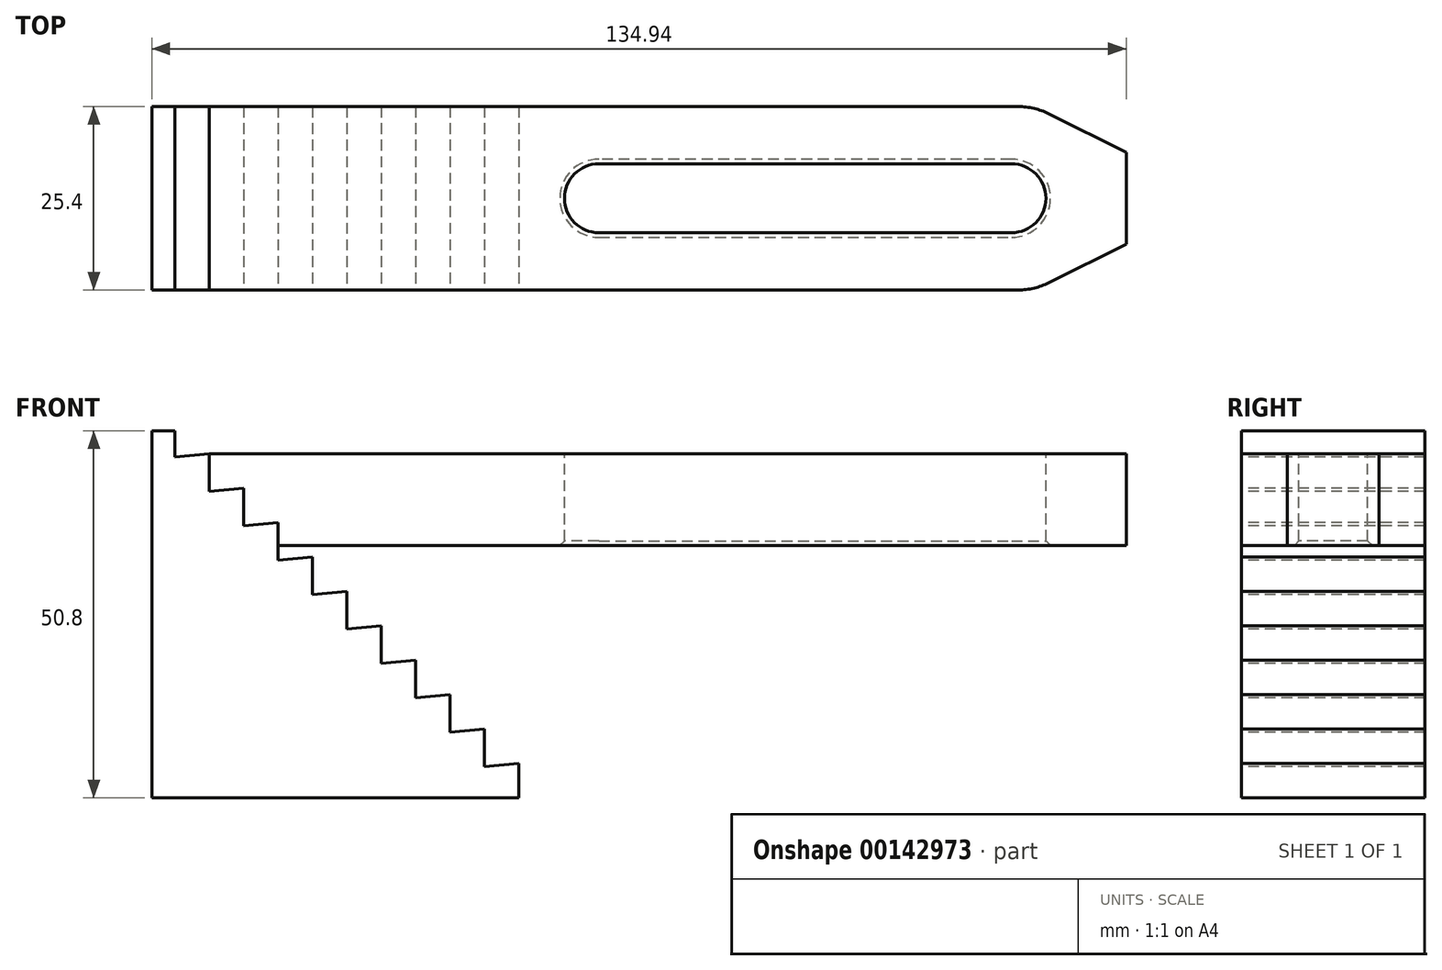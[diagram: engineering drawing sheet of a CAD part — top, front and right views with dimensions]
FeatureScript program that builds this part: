
annotation { "Feature Type Name" : "Feature", "Feature Type Description" : "" }
export const myFeature = defineFeature(function(context is Context, id is Id, definition is map)
    precondition{}
    {
        {
            var Q0;
            Q0=qCreatedBy(makeId("Top.planeOp"),FACE);
            var sketch = newSketch(context, id + "F0", { "sketchPlane" : qUnion([Q0])});
            skLineSegment(sketch, "E0.bottom", {"start": v(0, 0) * mm, "end": v(0, 0) * mm});
            skLineSegment(sketch, "E0.top", {"start": v(0, 0) * mm, "end": v(0, 0) * mm});
            skLineSegment(sketch, "E0.left", {"start": v(0, 0) * mm, "end": v(0, 0) * mm});
            skLineSegment(sketch, "E0.right", {"start": v(0, 0) * mm, "end": v(0, 0) * mm});
            skPoint(sketch, "E0.middle", {"position": v(0, 0) * mm});
            skLineSegment(sketch, "E1.bottom", {"start": v(25.4, 12.7) * mm, "end": v(-25.4, 12.7) * mm});
            skLineSegment(sketch, "E1.top", {"start": v(25.4, -12.7) * mm, "end": v(-25.4, -12.7) * mm});
            skLineSegment(sketch, "E1.left", {"start": v(25.4, 12.7) * mm, "end": v(25.4, -12.7) * mm});
            skLineSegment(sketch, "E1.right", {"start": v(-25.4, 12.7) * mm, "end": v(-25.4, -12.7) * mm});
            skSolve(sketch);
        }
        {
            var Q0;
            Q0 = qSketchRegion(id + "F0", true);
            extrude(context, id + "F1", {"entities" : qUnion([Q0]), "depth" : 50.8 * mm});
        }
        {
            var Q0;
            Q0=makeQuery(id+"F1.opExtrude","SWEPT_FACE",FACE,{"disambiguationData":[OSD([sQuery(id+"F0.wireOp",EDGE,"E1.top")])]});
            var sketch = newSketch(context, id + "F6", { "sketchPlane" : qUnion([Q0])});
            skLineSegment(sketch, "E2", {"start": v(-34.16, 4.76) * mm, "end": v(35.54, 4.76) * mm, "construction": true});
            skLineSegment(sketch, "E3", {"start": v(25.4, 4.76) * mm, "end": v(20.64, 4.35) * mm});
            skLineSegment(sketch, "E4.0.1.0", {"start": v(25.4, 9.53) * mm, "end": v(20.64, 9.1) * mm});
            skLineSegment(sketch, "E4.0.2.0", {"start": v(25.4, 14.29) * mm, "end": v(20.64, 13.87) * mm});
            skLineSegment(sketch, "E4.0.3.0", {"start": v(25.4, 19.05) * mm, "end": v(20.64, 18.63) * mm});
            skLineSegment(sketch, "E4.0.4.0", {"start": v(25.4, 23.81) * mm, "end": v(20.64, 23.4) * mm});
            skLineSegment(sketch, "E4.0.5.0", {"start": v(25.4, 28.58) * mm, "end": v(20.64, 28.16) * mm});
            skLineSegment(sketch, "E4.0.6.0", {"start": v(25.4, 33.34) * mm, "end": v(20.64, 32.92) * mm});
            skLineSegment(sketch, "E4.0.7.0", {"start": v(25.4, 38.1) * mm, "end": v(20.64, 37.68) * mm});
            skLineSegment(sketch, "E4.0.8.0", {"start": v(25.4, 42.86) * mm, "end": v(20.64, 42.45) * mm});
            skLineSegment(sketch, "E4.0.9.0", {"start": v(25.4, 47.63) * mm, "end": v(20.64, 47.2) * mm});
            skLineSegment(sketch, "E4.0.10.0", {"start": v(25.4, 52.39) * mm, "end": v(20.64, 51.97) * mm});
            skLineSegment(sketch, "E4.0.11.0", {"start": v(25.4, 57.15) * mm, "end": v(20.64, 56.73) * mm});
            skLineSegment(sketch, "E4.0.12.0", {"start": v(25.4, 61.91) * mm, "end": v(20.64, 61.5) * mm});
            skLineSegment(sketch, "E4.0.13.0", {"start": v(25.4, 66.68) * mm, "end": v(20.64, 66.26) * mm});
            skLineSegment(sketch, "E4.0.14.0", {"start": v(25.4, 71.44) * mm, "end": v(20.64, 71.02) * mm});
            skLineSegment(sketch, "E4.1.0.0", {"start": v(20.64, 4.76) * mm, "end": v(15.88, 4.35) * mm});
            skLineSegment(sketch, "E4.1.1.0", {"start": v(20.64, 9.53) * mm, "end": v(15.88, 9.1) * mm});
            skLineSegment(sketch, "E4.1.2.0", {"start": v(20.64, 14.29) * mm, "end": v(15.88, 13.87) * mm});
            skLineSegment(sketch, "E4.1.3.0", {"start": v(20.64, 19.05) * mm, "end": v(15.88, 18.63) * mm});
            skLineSegment(sketch, "E4.1.4.0", {"start": v(20.64, 23.81) * mm, "end": v(15.88, 23.4) * mm});
            skLineSegment(sketch, "E4.1.5.0", {"start": v(20.64, 28.58) * mm, "end": v(15.88, 28.16) * mm});
            skLineSegment(sketch, "E4.1.6.0", {"start": v(20.64, 33.34) * mm, "end": v(15.88, 32.92) * mm});
            skLineSegment(sketch, "E4.1.7.0", {"start": v(20.64, 38.1) * mm, "end": v(15.88, 37.68) * mm});
            skLineSegment(sketch, "E4.1.8.0", {"start": v(20.64, 42.86) * mm, "end": v(15.88, 42.45) * mm});
            skLineSegment(sketch, "E4.1.9.0", {"start": v(20.64, 47.63) * mm, "end": v(15.88, 47.2) * mm});
            skLineSegment(sketch, "E4.1.10.0", {"start": v(20.64, 52.39) * mm, "end": v(15.88, 51.97) * mm});
            skLineSegment(sketch, "E4.1.11.0", {"start": v(20.64, 57.15) * mm, "end": v(15.88, 56.73) * mm});
            skLineSegment(sketch, "E4.1.12.0", {"start": v(20.64, 61.91) * mm, "end": v(15.88, 61.5) * mm});
            skLineSegment(sketch, "E4.1.13.0", {"start": v(20.64, 66.68) * mm, "end": v(15.88, 66.26) * mm});
            skLineSegment(sketch, "E4.1.14.0", {"start": v(20.64, 71.44) * mm, "end": v(15.88, 71.02) * mm});
            skLineSegment(sketch, "E4.2.0.0", {"start": v(15.88, 4.76) * mm, "end": v(11.11, 4.35) * mm});
            skLineSegment(sketch, "E4.2.1.0", {"start": v(15.88, 9.53) * mm, "end": v(11.11, 9.1) * mm});
            skLineSegment(sketch, "E4.2.2.0", {"start": v(15.88, 14.29) * mm, "end": v(11.11, 13.87) * mm});
            skLineSegment(sketch, "E4.2.3.0", {"start": v(15.88, 19.05) * mm, "end": v(11.11, 18.63) * mm});
            skLineSegment(sketch, "E4.2.4.0", {"start": v(15.88, 23.81) * mm, "end": v(11.11, 23.4) * mm});
            skLineSegment(sketch, "E4.2.5.0", {"start": v(15.88, 28.58) * mm, "end": v(11.11, 28.16) * mm});
            skLineSegment(sketch, "E4.2.6.0", {"start": v(15.88, 33.34) * mm, "end": v(11.11, 32.92) * mm});
            skLineSegment(sketch, "E4.2.7.0", {"start": v(15.88, 38.1) * mm, "end": v(11.11, 37.68) * mm});
            skLineSegment(sketch, "E4.2.8.0", {"start": v(15.88, 42.86) * mm, "end": v(11.11, 42.45) * mm});
            skLineSegment(sketch, "E4.2.9.0", {"start": v(15.88, 47.63) * mm, "end": v(11.11, 47.2) * mm});
            skLineSegment(sketch, "E4.2.10.0", {"start": v(15.88, 52.39) * mm, "end": v(11.11, 51.97) * mm});
            skLineSegment(sketch, "E4.2.11.0", {"start": v(15.88, 57.15) * mm, "end": v(11.11, 56.73) * mm});
            skLineSegment(sketch, "E4.2.12.0", {"start": v(15.88, 61.91) * mm, "end": v(11.11, 61.5) * mm});
            skLineSegment(sketch, "E4.2.13.0", {"start": v(15.88, 66.68) * mm, "end": v(11.11, 66.26) * mm});
            skLineSegment(sketch, "E4.2.14.0", {"start": v(15.88, 71.44) * mm, "end": v(11.11, 71.02) * mm});
            skLineSegment(sketch, "E4.3.0.0", {"start": v(11.11, 4.76) * mm, "end": v(6.35, 4.35) * mm});
            skLineSegment(sketch, "E4.3.1.0", {"start": v(11.11, 9.53) * mm, "end": v(6.35, 9.1) * mm});
            skLineSegment(sketch, "E4.3.2.0", {"start": v(11.11, 14.29) * mm, "end": v(6.35, 13.87) * mm});
            skLineSegment(sketch, "E4.3.3.0", {"start": v(11.11, 19.05) * mm, "end": v(6.35, 18.63) * mm});
            skLineSegment(sketch, "E4.3.4.0", {"start": v(11.11, 23.81) * mm, "end": v(6.35, 23.4) * mm});
            skLineSegment(sketch, "E4.3.5.0", {"start": v(11.11, 28.58) * mm, "end": v(6.35, 28.16) * mm});
            skLineSegment(sketch, "E4.3.6.0", {"start": v(11.11, 33.34) * mm, "end": v(6.35, 32.92) * mm});
            skLineSegment(sketch, "E4.3.7.0", {"start": v(11.11, 38.1) * mm, "end": v(6.35, 37.68) * mm});
            skLineSegment(sketch, "E4.3.8.0", {"start": v(11.11, 42.86) * mm, "end": v(6.35, 42.45) * mm});
            skLineSegment(sketch, "E4.3.9.0", {"start": v(11.11, 47.63) * mm, "end": v(6.35, 47.2) * mm});
            skLineSegment(sketch, "E4.3.10.0", {"start": v(11.11, 52.39) * mm, "end": v(6.35, 51.97) * mm});
            skLineSegment(sketch, "E4.3.11.0", {"start": v(11.11, 57.15) * mm, "end": v(6.35, 56.73) * mm});
            skLineSegment(sketch, "E4.3.12.0", {"start": v(11.11, 61.91) * mm, "end": v(6.35, 61.5) * mm});
            skLineSegment(sketch, "E4.3.13.0", {"start": v(11.11, 66.68) * mm, "end": v(6.35, 66.26) * mm});
            skLineSegment(sketch, "E4.3.14.0", {"start": v(11.11, 71.44) * mm, "end": v(6.35, 71.02) * mm});
            skLineSegment(sketch, "E4.4.0.0", {"start": v(6.35, 4.76) * mm, "end": v(1.59, 4.35) * mm});
            skLineSegment(sketch, "E4.4.1.0", {"start": v(6.35, 9.53) * mm, "end": v(1.59, 9.1) * mm});
            skLineSegment(sketch, "E4.4.2.0", {"start": v(6.35, 14.29) * mm, "end": v(1.59, 13.87) * mm});
            skLineSegment(sketch, "E4.4.3.0", {"start": v(6.35, 19.05) * mm, "end": v(1.59, 18.63) * mm});
            skLineSegment(sketch, "E4.4.4.0", {"start": v(6.35, 23.81) * mm, "end": v(1.59, 23.4) * mm});
            skLineSegment(sketch, "E4.4.5.0", {"start": v(6.35, 28.58) * mm, "end": v(1.59, 28.16) * mm});
            skLineSegment(sketch, "E4.4.6.0", {"start": v(6.35, 33.34) * mm, "end": v(1.59, 32.92) * mm});
            skLineSegment(sketch, "E4.4.7.0", {"start": v(6.35, 38.1) * mm, "end": v(1.59, 37.68) * mm});
            skLineSegment(sketch, "E4.4.8.0", {"start": v(6.35, 42.86) * mm, "end": v(1.59, 42.45) * mm});
            skLineSegment(sketch, "E4.4.9.0", {"start": v(6.35, 47.63) * mm, "end": v(1.59, 47.2) * mm});
            skLineSegment(sketch, "E4.4.10.0", {"start": v(6.35, 52.39) * mm, "end": v(1.59, 51.97) * mm});
            skLineSegment(sketch, "E4.4.11.0", {"start": v(6.35, 57.15) * mm, "end": v(1.59, 56.73) * mm});
            skLineSegment(sketch, "E4.4.12.0", {"start": v(6.35, 61.91) * mm, "end": v(1.59, 61.5) * mm});
            skLineSegment(sketch, "E4.4.13.0", {"start": v(6.35, 66.68) * mm, "end": v(1.59, 66.26) * mm});
            skLineSegment(sketch, "E4.4.14.0", {"start": v(6.35, 71.44) * mm, "end": v(1.59, 71.02) * mm});
            skLineSegment(sketch, "E4.5.0.0", {"start": v(1.59, 4.76) * mm, "end": v(-3.17, 4.35) * mm});
            skLineSegment(sketch, "E4.5.1.0", {"start": v(1.59, 9.53) * mm, "end": v(-3.17, 9.1) * mm});
            skLineSegment(sketch, "E4.5.2.0", {"start": v(1.59, 14.29) * mm, "end": v(-3.17, 13.87) * mm});
            skLineSegment(sketch, "E4.5.3.0", {"start": v(1.59, 19.05) * mm, "end": v(-3.17, 18.63) * mm});
            skLineSegment(sketch, "E4.5.4.0", {"start": v(1.59, 23.81) * mm, "end": v(-3.17, 23.4) * mm});
            skLineSegment(sketch, "E4.5.5.0", {"start": v(1.59, 28.58) * mm, "end": v(-3.17, 28.16) * mm});
            skLineSegment(sketch, "E4.5.6.0", {"start": v(1.59, 33.34) * mm, "end": v(-3.17, 32.92) * mm});
            skLineSegment(sketch, "E4.5.7.0", {"start": v(1.59, 38.1) * mm, "end": v(-3.17, 37.68) * mm});
            skLineSegment(sketch, "E4.5.8.0", {"start": v(1.59, 42.86) * mm, "end": v(-3.17, 42.45) * mm});
            skLineSegment(sketch, "E4.5.9.0", {"start": v(1.59, 47.63) * mm, "end": v(-3.17, 47.2) * mm});
            skLineSegment(sketch, "E4.5.10.0", {"start": v(1.59, 52.39) * mm, "end": v(-3.17, 51.97) * mm});
            skLineSegment(sketch, "E4.5.11.0", {"start": v(1.59, 57.15) * mm, "end": v(-3.17, 56.73) * mm});
            skLineSegment(sketch, "E4.5.12.0", {"start": v(1.59, 61.91) * mm, "end": v(-3.17, 61.5) * mm});
            skLineSegment(sketch, "E4.5.13.0", {"start": v(1.59, 66.68) * mm, "end": v(-3.17, 66.26) * mm});
            skLineSegment(sketch, "E4.5.14.0", {"start": v(1.59, 71.44) * mm, "end": v(-3.17, 71.02) * mm});
            skLineSegment(sketch, "E4.6.0.0", {"start": v(-3.17, 4.76) * mm, "end": v(-7.94, 4.35) * mm});
            skLineSegment(sketch, "E4.6.1.0", {"start": v(-3.17, 9.53) * mm, "end": v(-7.94, 9.1) * mm});
            skLineSegment(sketch, "E4.6.2.0", {"start": v(-3.17, 14.29) * mm, "end": v(-7.94, 13.87) * mm});
            skLineSegment(sketch, "E4.6.3.0", {"start": v(-3.17, 19.05) * mm, "end": v(-7.94, 18.63) * mm});
            skLineSegment(sketch, "E4.6.4.0", {"start": v(-3.17, 23.81) * mm, "end": v(-7.94, 23.4) * mm});
            skLineSegment(sketch, "E4.6.5.0", {"start": v(-3.17, 28.58) * mm, "end": v(-7.94, 28.16) * mm});
            skLineSegment(sketch, "E4.6.6.0", {"start": v(-3.17, 33.34) * mm, "end": v(-7.94, 32.92) * mm});
            skLineSegment(sketch, "E4.6.7.0", {"start": v(-3.17, 38.1) * mm, "end": v(-7.94, 37.68) * mm});
            skLineSegment(sketch, "E4.6.8.0", {"start": v(-3.17, 42.86) * mm, "end": v(-7.94, 42.45) * mm});
            skLineSegment(sketch, "E4.6.9.0", {"start": v(-3.17, 47.63) * mm, "end": v(-7.94, 47.2) * mm});
            skLineSegment(sketch, "E4.6.10.0", {"start": v(-3.17, 52.39) * mm, "end": v(-7.94, 51.97) * mm});
            skLineSegment(sketch, "E4.6.11.0", {"start": v(-3.17, 57.15) * mm, "end": v(-7.94, 56.73) * mm});
            skLineSegment(sketch, "E4.6.12.0", {"start": v(-3.17, 61.91) * mm, "end": v(-7.94, 61.5) * mm});
            skLineSegment(sketch, "E4.6.13.0", {"start": v(-3.17, 66.68) * mm, "end": v(-7.94, 66.26) * mm});
            skLineSegment(sketch, "E4.6.14.0", {"start": v(-3.17, 71.44) * mm, "end": v(-7.94, 71.02) * mm});
            skLineSegment(sketch, "E4.7.0.0", {"start": v(-7.94, 4.76) * mm, "end": v(-12.7, 4.35) * mm});
            skLineSegment(sketch, "E4.7.1.0", {"start": v(-7.94, 9.53) * mm, "end": v(-12.7, 9.1) * mm});
            skLineSegment(sketch, "E4.7.2.0", {"start": v(-7.94, 14.29) * mm, "end": v(-12.7, 13.87) * mm});
            skLineSegment(sketch, "E4.7.3.0", {"start": v(-7.94, 19.05) * mm, "end": v(-12.7, 18.63) * mm});
            skLineSegment(sketch, "E4.7.4.0", {"start": v(-7.94, 23.81) * mm, "end": v(-12.7, 23.4) * mm});
            skLineSegment(sketch, "E4.7.5.0", {"start": v(-7.94, 28.58) * mm, "end": v(-12.7, 28.16) * mm});
            skLineSegment(sketch, "E4.7.6.0", {"start": v(-7.94, 33.34) * mm, "end": v(-12.7, 32.92) * mm});
            skLineSegment(sketch, "E4.7.7.0", {"start": v(-7.94, 38.1) * mm, "end": v(-12.7, 37.68) * mm});
            skLineSegment(sketch, "E4.7.8.0", {"start": v(-7.94, 42.86) * mm, "end": v(-12.7, 42.45) * mm});
            skLineSegment(sketch, "E4.7.9.0", {"start": v(-7.94, 47.63) * mm, "end": v(-12.7, 47.2) * mm});
            skLineSegment(sketch, "E4.7.10.0", {"start": v(-7.94, 52.39) * mm, "end": v(-12.7, 51.97) * mm});
            skLineSegment(sketch, "E4.7.11.0", {"start": v(-7.94, 57.15) * mm, "end": v(-12.7, 56.73) * mm});
            skLineSegment(sketch, "E4.7.12.0", {"start": v(-7.94, 61.91) * mm, "end": v(-12.7, 61.5) * mm});
            skLineSegment(sketch, "E4.7.13.0", {"start": v(-7.94, 66.68) * mm, "end": v(-12.7, 66.26) * mm});
            skLineSegment(sketch, "E4.7.14.0", {"start": v(-7.94, 71.44) * mm, "end": v(-12.7, 71.02) * mm});
            skLineSegment(sketch, "E4.8.0.0", {"start": v(-12.7, 4.76) * mm, "end": v(-17.46, 4.35) * mm});
            skLineSegment(sketch, "E4.8.1.0", {"start": v(-12.7, 9.53) * mm, "end": v(-17.46, 9.1) * mm});
            skLineSegment(sketch, "E4.8.2.0", {"start": v(-12.7, 14.29) * mm, "end": v(-17.46, 13.87) * mm});
            skLineSegment(sketch, "E4.8.3.0", {"start": v(-12.7, 19.05) * mm, "end": v(-17.46, 18.63) * mm});
            skLineSegment(sketch, "E4.8.4.0", {"start": v(-12.7, 23.81) * mm, "end": v(-17.46, 23.4) * mm});
            skLineSegment(sketch, "E4.8.5.0", {"start": v(-12.7, 28.58) * mm, "end": v(-17.46, 28.16) * mm});
            skLineSegment(sketch, "E4.8.6.0", {"start": v(-12.7, 33.34) * mm, "end": v(-17.46, 32.92) * mm});
            skLineSegment(sketch, "E4.8.7.0", {"start": v(-12.7, 38.1) * mm, "end": v(-17.46, 37.68) * mm});
            skLineSegment(sketch, "E4.8.8.0", {"start": v(-12.7, 42.86) * mm, "end": v(-17.46, 42.45) * mm});
            skLineSegment(sketch, "E4.8.9.0", {"start": v(-12.7, 47.63) * mm, "end": v(-17.46, 47.2) * mm});
            skLineSegment(sketch, "E4.8.10.0", {"start": v(-12.7, 52.39) * mm, "end": v(-17.46, 51.97) * mm});
            skLineSegment(sketch, "E4.8.11.0", {"start": v(-12.7, 57.15) * mm, "end": v(-17.46, 56.73) * mm});
            skLineSegment(sketch, "E4.8.12.0", {"start": v(-12.7, 61.91) * mm, "end": v(-17.46, 61.5) * mm});
            skLineSegment(sketch, "E4.8.13.0", {"start": v(-12.7, 66.68) * mm, "end": v(-17.46, 66.26) * mm});
            skLineSegment(sketch, "E4.8.14.0", {"start": v(-12.7, 71.44) * mm, "end": v(-17.46, 71.02) * mm});
            skLineSegment(sketch, "E4.9.0.0", {"start": v(-17.46, 4.76) * mm, "end": v(-22.22, 4.35) * mm});
            skLineSegment(sketch, "E4.9.1.0", {"start": v(-17.46, 9.53) * mm, "end": v(-22.22, 9.1) * mm});
            skLineSegment(sketch, "E4.9.2.0", {"start": v(-17.46, 14.29) * mm, "end": v(-22.22, 13.87) * mm});
            skLineSegment(sketch, "E4.9.3.0", {"start": v(-17.46, 19.05) * mm, "end": v(-22.22, 18.63) * mm});
            skLineSegment(sketch, "E4.9.4.0", {"start": v(-17.46, 23.81) * mm, "end": v(-22.22, 23.4) * mm});
            skLineSegment(sketch, "E4.9.5.0", {"start": v(-17.46, 28.58) * mm, "end": v(-22.22, 28.16) * mm});
            skLineSegment(sketch, "E4.9.6.0", {"start": v(-17.46, 33.34) * mm, "end": v(-22.22, 32.92) * mm});
            skLineSegment(sketch, "E4.9.7.0", {"start": v(-17.46, 38.1) * mm, "end": v(-22.22, 37.68) * mm});
            skLineSegment(sketch, "E4.9.8.0", {"start": v(-17.46, 42.86) * mm, "end": v(-22.22, 42.45) * mm});
            skLineSegment(sketch, "E4.9.9.0", {"start": v(-17.46, 47.63) * mm, "end": v(-22.22, 47.2) * mm});
            skLineSegment(sketch, "E4.9.10.0", {"start": v(-17.46, 52.39) * mm, "end": v(-22.22, 51.97) * mm});
            skLineSegment(sketch, "E4.9.11.0", {"start": v(-17.46, 57.15) * mm, "end": v(-22.22, 56.73) * mm});
            skLineSegment(sketch, "E4.9.12.0", {"start": v(-17.46, 61.91) * mm, "end": v(-22.22, 61.5) * mm});
            skLineSegment(sketch, "E4.9.13.0", {"start": v(-17.46, 66.68) * mm, "end": v(-22.22, 66.26) * mm});
            skLineSegment(sketch, "E4.9.14.0", {"start": v(-17.46, 71.44) * mm, "end": v(-22.22, 71.02) * mm});
            skLineSegment(sketch, "E4.direction1", {"start": v(20.64, 4.35) * mm, "end": v(15.88, 4.35) * mm, "construction": true});
            skLineSegment(sketch, "E4.direction2", {"start": v(20.64, 4.35) * mm, "end": v(20.64, 9.1) * mm, "construction": true});
            skSolve(sketch);
        }
        {
            var Q0;
            Q0=makeQuery(id+"F1.opExtrude","SWEPT_FACE",FACE,{"disambiguationData":[OSD([sQuery(id+"F0.wireOp",EDGE,"E1.top")])]});
            cPlane(context, id + "F2", {"entities" : qUnion([Q0]), "cplaneType" : CPlaneType.OFFSET, "offset" : 0 * mm, "width" : 152.4 * mm, "height" : 152.4 * mm});
        }
        {
            var Q0;
            Q0=qCreatedBy(id+"F2.planeOp",FACE);
            var sketch = newSketch(context, id + "F7", { "sketchPlane" : qUnion([Q0])});
            skLineSegment(sketch, "E5.0", {"start": v(25.4, 4.76) * mm, "end": v(20.64, 4.35) * mm});
            skLineSegment(sketch, "E6.1", {"start": v(20.64, 9.53) * mm, "end": v(15.88, 9.1) * mm});
            skLineSegment(sketch, "E7.0", {"start": v(15.88, 14.29) * mm, "end": v(11.11, 13.87) * mm});
            skLineSegment(sketch, "E8.1", {"start": v(11.11, 19.05) * mm, "end": v(6.35, 18.63) * mm});
            skLineSegment(sketch, "E9.0", {"start": v(6.35, 23.81) * mm, "end": v(1.59, 23.4) * mm});
            skLineSegment(sketch, "E10.1", {"start": v(1.59, 28.58) * mm, "end": v(-3.17, 28.16) * mm});
            skLineSegment(sketch, "E11.0", {"start": v(-3.17, 33.34) * mm, "end": v(-7.94, 32.92) * mm});
            skLineSegment(sketch, "E12.1", {"start": v(-7.94, 38.1) * mm, "end": v(-12.7, 37.68) * mm});
            skLineSegment(sketch, "E13.0.12", {"start": v(25.4, 47.63) * mm, "end": v(25.4, 47.63) * mm});
            skLineSegment(sketch, "E13.0.13", {"start": v(25.4, 47.63) * mm, "end": v(25.4, 47.63) * mm});
            skLineSegment(sketch, "E14.0", {"start": v(-12.7, 42.86) * mm, "end": v(-17.46, 42.45) * mm});
            skLineSegment(sketch, "E15.0", {"start": v(-17.46, 47.63) * mm, "end": v(-22.22, 47.2) * mm});
            skLineSegment(sketch, "E16", {"start": v(20.64, 4.35) * mm, "end": v(20.64, 9.53) * mm});
            skLineSegment(sketch, "E17", {"start": v(15.88, 14.29) * mm, "end": v(15.88, 9.1) * mm});
            skLineSegment(sketch, "E18", {"start": v(1.59, 28.58) * mm, "end": v(1.59, 23.4) * mm});
            skLineSegment(sketch, "E19", {"start": v(6.35, 23.81) * mm, "end": v(6.35, 18.63) * mm});
            skLineSegment(sketch, "E20", {"start": v(11.11, 19.05) * mm, "end": v(11.11, 13.87) * mm});
            skLineSegment(sketch, "E21", {"start": v(-17.46, 47.63) * mm, "end": v(-17.46, 42.45) * mm});
            skLineSegment(sketch, "E22", {"start": v(-7.94, 38.1) * mm, "end": v(-7.94, 32.92) * mm});
            skLineSegment(sketch, "E23", {"start": v(-12.7, 42.86) * mm, "end": v(-12.7, 37.68) * mm});
            skLineSegment(sketch, "E24", {"start": v(-3.17, 33.34) * mm, "end": v(-3.17, 28.16) * mm});
            skPoint(sketch, "E13.0.0.start.orphan", {"position": v(-25.4, 0) * mm});
            skPoint(sketch, "E13.0.3.start.orphan", {"position": v(25.4, 9.53) * mm});
            skPoint(sketch, "E13.0.4.start.orphan", {"position": v(25.4, 14.29) * mm});
            skPoint(sketch, "E13.0.5.start.orphan", {"position": v(25.4, 19.05) * mm});
            skPoint(sketch, "E13.0.6.start.orphan", {"position": v(25.4, 23.81) * mm});
            skPoint(sketch, "E13.0.15.end.orphan", {"position": v(20.64, 57.15) * mm});
            skPoint(sketch, "E13.0.7.start.orphan", {"position": v(25.4, 28.58) * mm});
            skPoint(sketch, "E13.0.8.end.orphan", {"position": v(25.4, 38.1) * mm});
            skPoint(sketch, "E13.0.8.start.orphan", {"position": v(25.4, 33.34) * mm});
            skPoint(sketch, "E13.0.10.start.orphan", {"position": v(25.4, 42.86) * mm});
            skPoint(sketch, "E13.0.14.end.orphan", {"position": v(25.4, 50.8) * mm});
            skPoint(sketch, "E13.0.11.start.orphan", {"position": v(25.4, 47.63) * mm});
            skPoint(sketch, "E13.0.1.end.orphan", {"position": v(25.4, 4.76) * mm});
            skPoint(sketch, "E13.0.1.start.orphan", {"position": v(25.4, 0) * mm});
            skLineSegment(sketch, "E25", {"start": v(25.4, 4.76) * mm, "end": v(25.4, 68.26) * mm});
            skLineSegment(sketch, "E26", {"start": v(25.4, 68.26) * mm, "end": v(-22.22, 68.26) * mm});
            skLineSegment(sketch, "E27", {"start": v(-22.22, 68.26) * mm, "end": v(-22.22, 68.26) * mm});
            skLineSegment(sketch, "E28", {"start": v(-22.22, 68.26) * mm, "end": v(-22.22, 47.2) * mm});
            skSolve(sketch);
        }
        {
            var Q0;
            Q0 = qSketchRegion(id + "F7", true);
            extrude(context, id + "F8", {"entities" : qUnion([Q0]), "operationType" : NewBodyOperationType.REMOVE, "endBound" : BoundingType.THROUGH_ALL, "oppositeDirection" : true, "depth" : 25.4 * mm});
        }
        {
            var Q0;
            Q0=qCreatedBy(makeId("Top.planeOp"),FACE);
            cPlane(context, id + "F3", {"entities" : qUnion([Q0]), "cplaneType" : CPlaneType.OFFSET, "offset" : 47.62 * mm, "width" : 152.4 * mm, "height" : 152.4 * mm});
        }
        {
            var Q0;
            Q0=qCreatedBy(id+"F3.planeOp",FACE);
            var sketch = newSketch(context, id + "F9", { "sketchPlane" : qUnion([Q0])});
            skLineSegment(sketch, "E29.bottom", {"start": v(-17.46, 12.7) * mm, "end": v(96.84, 12.7) * mm});
            skLineSegment(sketch, "E29.top", {"start": v(-17.46, -12.7) * mm, "end": v(96.84, -12.7) * mm});
            skLineSegment(sketch, "E29.left", {"start": v(-17.46, 12.7) * mm, "end": v(-17.46, -12.7) * mm});
            skPoint(sketch, "E30", {"position": v(-17.46, 12.7) * mm});
            skPoint(sketch, "E31", {"position": v(-17.46, -12.7) * mm});
            skPoint(sketch, "E32", {"position": v(109.54, 0) * mm});
            skPoint(sketch, "E33", {"position": v(96.84, -12.7) * mm});
            skPoint(sketch, "E34.orphan", {"position": v(109.54, -12.7) * mm});
            skPoint(sketch, "E35", {"position": v(96.84, 12.7) * mm});
            skLineSegment(sketch, "E36", {"start": v(109.54, 0) * mm, "end": v(109.54, 6.35) * mm});
            skLineSegment(sketch, "E37", {"start": v(109.54, 0) * mm, "end": v(109.54, -6.35) * mm});
            skPoint(sketch, "E38.start.orphan", {"position": v(109.54, 12.7) * mm});
            skLineSegment(sketch, "E39", {"start": v(96.84, 12.7) * mm, "end": v(109.54, 6.35) * mm});
            skLineSegment(sketch, "E40", {"start": v(96.84, -12.7) * mm, "end": v(109.54, -6.35) * mm});
            skSolve(sketch);
        }
        {
            var Q0;
            Q0 = qSketchRegion(id + "F9", true);
            extrude(context, id + "F10", {"entities" : qUnion([Q0]), "oppositeDirection" : true, "depth" : 12.7 * mm});
        }
        {
            var Q0;
            Q0=makeQuery(id+"F9.imprint","IMPRINT",FACE,{"disambiguationData":[TD([[makeQuery(id+"F9.imprint","IMPRINT",EDGE,{"derivedFrom":sQuery(id+"F9.wireOp",EDGE,"E29.bottom")}),-1.0]])]});
            var sketch = newSketch(context, id + "F11", { "sketchPlane" : qUnion([Q0])});
            skLineSegment(sketch, "E41", {"start": v(31.75, 24.2) * mm, "end": v(31.75, -24.2) * mm, "construction": true});
            skPoint(sketch, "E42", {"position": v(31.75, 0) * mm});
            skLineSegment(sketch, "E43", {"start": v(36.51, 0) * mm, "end": v(93.66, 0) * mm});
            skLineSegment(sketch, "E44", {"start": v(36.51, 24.2) * mm, "end": v(36.51, -24.2) * mm, "construction": true});
            skPoint(sketch, "E45", {"position": v(93.66, 0) * mm});
            skPoint(sketch, "E46", {"position": v(36.51, 0) * mm});
            skArc(sketch, "E47.0.startCap", {"start": v(36.51, -4.76) * mm, "mid": v(31.75, 0) * mm, "end": v(36.51, 4.76) * mm});
            skArc(sketch, "E47.0.endCap", {"start": v(93.66, 4.76) * mm, "mid": v(98.43, 0) * mm, "end": v(93.66, -4.76) * mm});
            skLineSegment(sketch, "E47.0.left", {"start": v(36.51, 4.76) * mm, "end": v(93.66, 4.76) * mm});
            skLineSegment(sketch, "E47.0.right", {"start": v(36.51, -4.76) * mm, "end": v(93.66, -4.76) * mm});
            skSolve(sketch);
        }
        {
            var Q0;
            Q0 = qSketchRegion(id + "F11", true);
            extrude(context, id + "F4", {"entities" : qUnion([Q0]), "operationType" : NewBodyOperationType.REMOVE, "endBound" : BoundingType.THROUGH_ALL, "oppositeDirection" : true, "depth" : 25.4 * mm});
        }
        {
            var Q0;
            Q0=makeQuery(id+"F1.opExtrude","SWEPT_BODY",BODY,{"disambiguationData":[OSD([sQuery(id+"F0.wireOp",EDGE,"E1.bottom"),sQuery(id+"F0.wireOp",EDGE,"E1.top"),sQuery(id+"F0.wireOp",EDGE,"E1.left"),sQuery(id+"F0.wireOp",EDGE,"E1.right")])]});
            var Q1;
            Q1=makeQuery(id+"F10.opExtrude","SWEPT_BODY",BODY,{"disambiguationData":[OSD([sQuery(id+"F9.wireOp",EDGE,"E29.bottom"),sQuery(id+"F9.wireOp",EDGE,"E29.top"),sQuery(id+"F9.wireOp",EDGE,"E29.left"),sQuery(id+"F9.wireOp",EDGE,"E36"),sQuery(id+"F9.wireOp",EDGE,"E37"),sQuery(id+"F9.wireOp",EDGE,"E39"),sQuery(id+"F9.wireOp",EDGE,"E40")])]});
            booleanBodies(context, id + "F5", {"operationType" : BooleanOperationType.SUBTRACTION, "tools" : qUnion([Q0]), "targets" : qUnion([Q1]), "keepTools" : true});
        }
        {
            var Q0;
            Q0=makeQuery(id+"F4.boolean.opBoolean","COPY",EDGE,{"derivedFrom":makeQuery(id+"F4.opExtrude","CAP_EDGE",EDGE,{"disambiguationData":[OSD([sQuery(id+"F11.wireOp",EDGE,"E47.0.left")])],"isStart":true})});
            var Q1;
            Q1=makeQuery(id+"F4.boolean.opBoolean","INTERSECT",EDGE,{"derivedFrom":[makeQuery(id+"F10.opExtrude","CAP_FACE",FACE,{"disambiguationData":[OSD([sQuery(id+"F9.wireOp",EDGE,"E29.bottom"),sQuery(id+"F9.wireOp",EDGE,"E29.top"),sQuery(id+"F9.wireOp",EDGE,"E29.left"),sQuery(id+"F9.wireOp",EDGE,"E36"),sQuery(id+"F9.wireOp",EDGE,"E37"),sQuery(id+"F9.wireOp",EDGE,"E39"),sQuery(id+"F9.wireOp",EDGE,"E40")])],"isStart":false}),makeQuery(id+"F4.opExtrude","SWEPT_FACE",FACE,{"disambiguationData":[OSD([sQuery(id+"F11.wireOp",EDGE,"E47.0.right")])]})]});
            chamfer(context, id + "F12", {"entities" : qUnion([Q0, Q1]), "width" : 0.64 * mm, "tangentPropagation" : true});
        }
        {
            var Q0;
            Q0=makeQuery(id+"F10.opExtrude","SWEPT_EDGE",EDGE,{"disambiguationData":[OSD([sQuery(id+"F9.wireOp",EDGE,"E29.top"),sQuery(id+"F9.wireOp",EDGE,"E40")])]});
            var Q1;
            Q1=makeQuery(id+"F10.opExtrude","SWEPT_EDGE",EDGE,{"disambiguationData":[OSD([sQuery(id+"F9.wireOp",EDGE,"E29.bottom"),sQuery(id+"F9.wireOp",EDGE,"E39")])]});
            fillet(context, id + "F13", {"entities" : qUnion([Q0, Q1]), "radius" : 9.52 * mm, "tangentPropagation" : true, "allowEdgeOverflow" : false});
        }
    });
